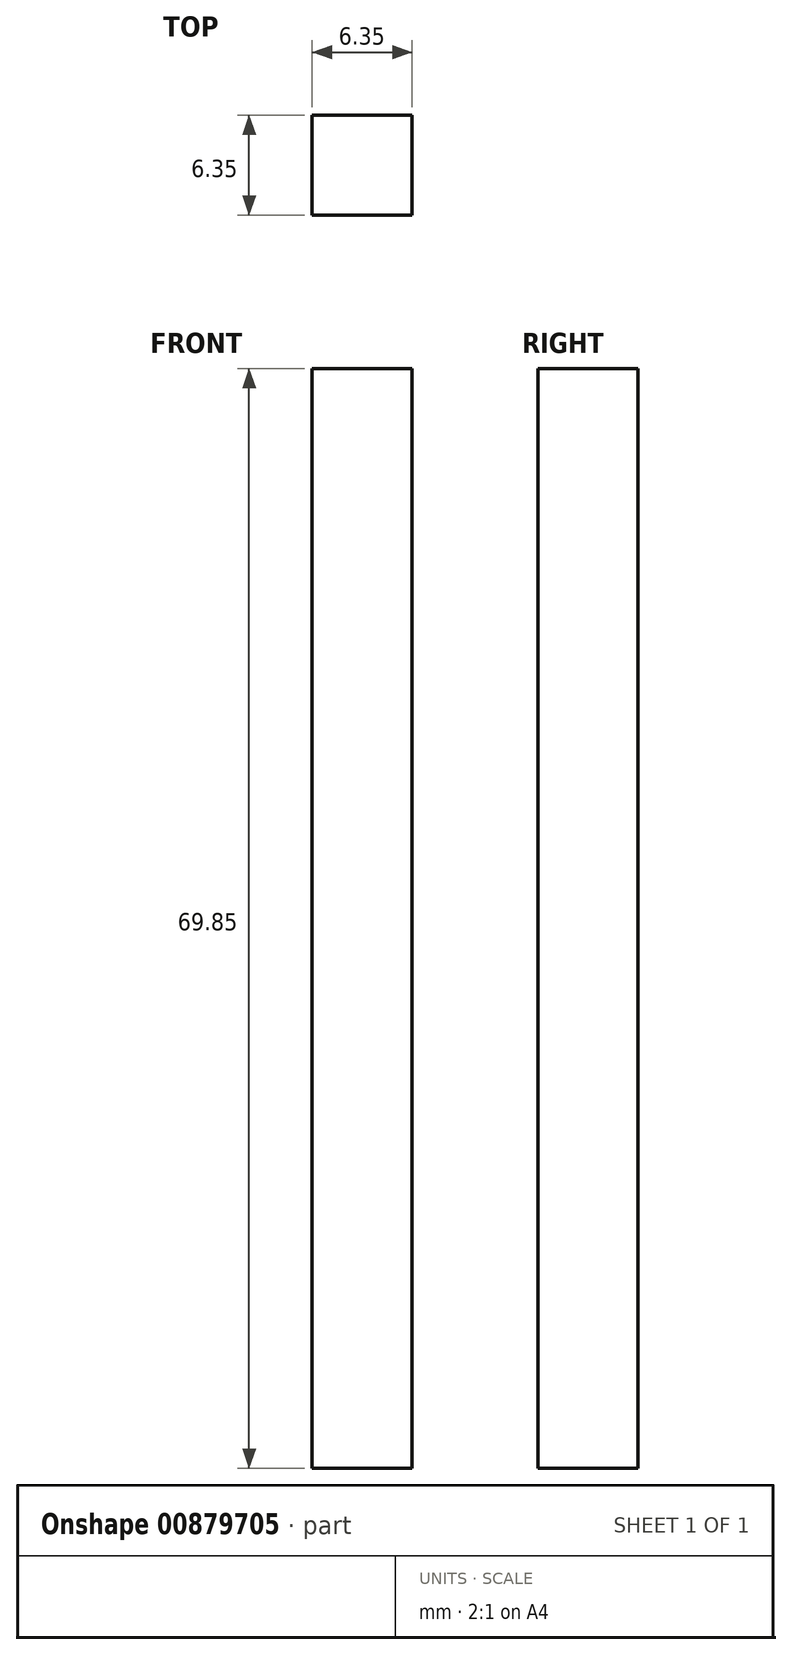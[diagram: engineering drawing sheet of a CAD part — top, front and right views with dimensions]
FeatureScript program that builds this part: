
annotation { "Feature Type Name" : "Feature", "Feature Type Description" : "" }
export const myFeature = defineFeature(function(context is Context, id is Id, definition is map)
    precondition{}
    {
        {
            var Q0;
            Q0=qCreatedBy(makeId("Front.planeOp"),FACE);
            var sketch = newSketch(context, id + "F0", { "sketchPlane" : qUnion([Q0])});
            skLineSegment(sketch, "E0.bottom", {"start": v(-53.44, 69.85) * mm, "end": v(-47.09, 69.85) * mm});
            skLineSegment(sketch, "E0.top", {"start": v(-53.44, 0) * mm, "end": v(-47.09, 0) * mm});
            skLineSegment(sketch, "E0.left", {"start": v(-53.44, 69.85) * mm, "end": v(-53.44, 0) * mm});
            skLineSegment(sketch, "E0.right", {"start": v(-47.09, 69.85) * mm, "end": v(-47.09, 0) * mm});
            skSolve(sketch);
        }
        {
            var Q0;
            Q0 = qSketchRegion(id + "F0", true);
            extrude(context, id + "F1", {"entities" : qUnion([Q0]), "depth" : 6.35 * mm, "offsetDistance" : 25.4 * mm});
        }
    });
